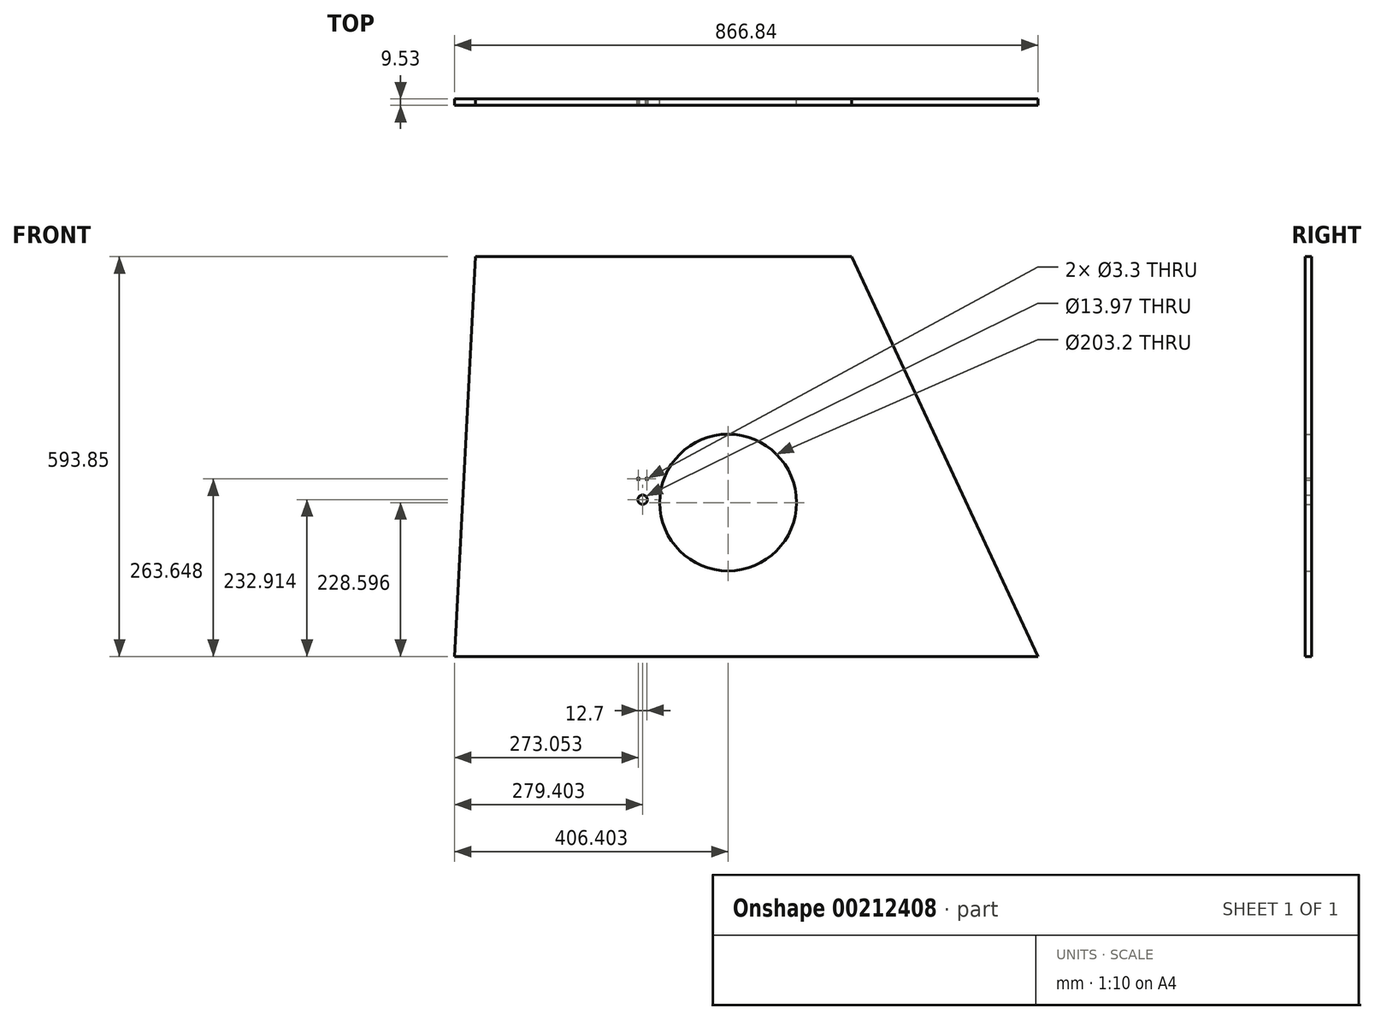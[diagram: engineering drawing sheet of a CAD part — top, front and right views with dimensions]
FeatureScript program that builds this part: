
annotation { "Feature Type Name" : "Feature", "Feature Type Description" : "" }
export const myFeature = defineFeature(function(context is Context, id is Id, definition is map)
    precondition{}
    {
        {
            var Q0;
            Q0=qCreatedBy(makeId("Front.planeOp"),FACE);
            var sketch = newSketch(context, id + "F0", { "sketchPlane" : qUnion([Q0])});
            skLineSegment(sketch, "E0", {"start": v(-518.92, -288.64) * mm, "end": v(-487.8, 305.2) * mm});
            skLineSegment(sketch, "E1", {"start": v(-487.8, 305.2) * mm, "end": v(71, 305.2) * mm});
            skLineSegment(sketch, "E2", {"start": v(71, 305.2) * mm, "end": v(347.92, -288.64) * mm});
            skLineSegment(sketch, "E3", {"start": v(347.92, -288.64) * mm, "end": v(-518.92, -288.64) * mm});
            skCircle(sketch, "E4", {"center": v(-112.52, -60.04) * mm, "radius": 101.6 * mm});
            skCircle(sketch, "E5", {"center": v(-239.52, -55.73) * mm, "radius": 6.99 * mm});
            skCircle(sketch, "E6", {"center": v(-245.87, -25) * mm, "radius": 1.65 * mm});
            skCircle(sketch, "E7", {"center": v(-233.17, -25) * mm, "radius": 1.65 * mm});
            skLineSegment(sketch, "E8", {"start": v(71, 305.2) * mm, "end": v(-518.92, -288.64) * mm, "construction": true});
            skSolve(sketch);
        }
        {
            var Q0;
            Q0 = qSketchRegion(id + "F0", true);
            extrude(context, id + "F1", {"entities" : qUnion([Q0]), "depth" : 9.52 * mm});
        }
    });
